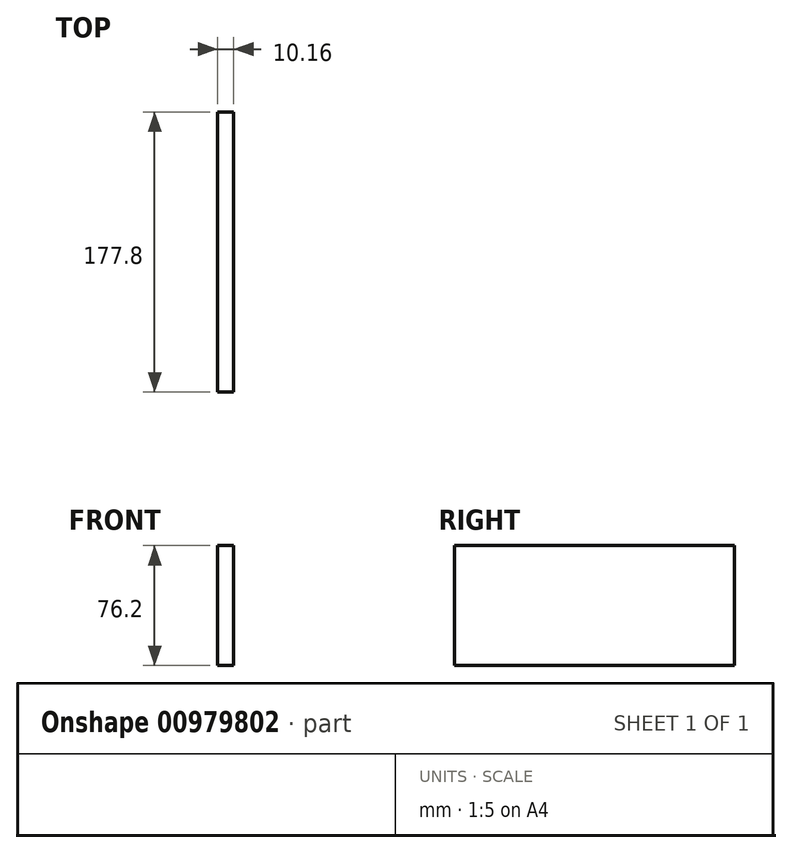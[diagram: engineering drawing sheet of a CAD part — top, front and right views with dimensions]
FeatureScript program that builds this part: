
annotation { "Feature Type Name" : "Feature", "Feature Type Description" : "" }
export const myFeature = defineFeature(function(context is Context, id is Id, definition is map)
    precondition{}
    {
        {
            var Q0;
            Q0=qCreatedBy(makeId("Right.planeOp"),FACE);
            var sketch = newSketch(context, id + "F0", { "sketchPlane" : qUnion([Q0])});
            skLineSegment(sketch, "E0.bottom", {"start": v(-88.9, 38.1) * mm, "end": v(88.9, 38.1) * mm});
            skLineSegment(sketch, "E0.top", {"start": v(-88.9, -38.1) * mm, "end": v(88.9, -38.1) * mm});
            skLineSegment(sketch, "E0.left", {"start": v(-88.9, 38.1) * mm, "end": v(-88.9, -38.1) * mm});
            skLineSegment(sketch, "E0.right", {"start": v(88.9, 38.1) * mm, "end": v(88.9, -38.1) * mm});
            skPoint(sketch, "E0.middle", {"position": v(0, 0) * mm});
            skSolve(sketch);
        }
        {
            var Q0;
            Q0=makeQuery(id+"F0.imprint","IMPRINT",FACE,{"disambiguationData":[TD([[makeQuery(id+"F0.imprint","IMPRINT",EDGE,{"derivedFrom":sQuery(id+"F0.wireOp",EDGE,"E0.bottom")}),-1.0]])]});
            extrude(context, id + "F1", {"entities" : qUnion([Q0]), "depth" : 10.16 * mm, "offsetDistance" : 25.4 * mm});
        }
    });
